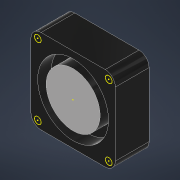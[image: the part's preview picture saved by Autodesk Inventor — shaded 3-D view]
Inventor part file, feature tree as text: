
AUTODESK INVENTOR PART (.ipt)
format: ipt  version: 2021 (Build 250183000, 183)  size: 166,400 bytes
history: native  units: mm
features: extrude x4, sketch x4, reference x4, other x3
ambient origin geometry x8: Origin, YZ Plane, XZ Plane, XY Plane, X Axis, Y Axis, Z Axis, Center Point
bodies: Solid1 (feature_tree)
feature tree (15):
  extrude  "Extrusion1"  Depth=25.0mm
  extrude  "Extrusion2"  Depth=10.0mm TaperAngle=0.0deg
  extrude  "Extrusion3"  Depth=4.0mm TaperAngle=0.0deg
  extrude  "Extrusion4"  Depth=10.0mm TaperAngle=0.0deg
  sketch  "Sketch1"  dims[d0=25.0mm d1=25.0mm]
  reference  "Reference1"
  reference  "Reference2"
  reference  "Reference3"
  reference  "Reference4"
  sketch  "Sketch2"  dims[d2=3.0mm d3=10.0mm d4=0.0mm]
  sketch  "Sketch3"  dims[d5=21.0mm d6=4.0mm d7=0.0mm]
  sketch  "Sketch4"  dims[d8=16.0mm d9=10.0mm d10=0.0mm d11=5.0mm d12=19.0mm d13=19.0mm d14=20.0mm d16=19.0mm d17=20.0mm d19=19.0mm d22=1.0mm d23=0.0mm]
  parser-record x1  (decoder bookkeeping rows leaked as tree rows — omitted from the tree; the rows remain in map.json)
  other  "esc.iam"
  other  "heatsink:1"
note: 1 file-system path scrubbed to <path> (originals preserved in map.json)
